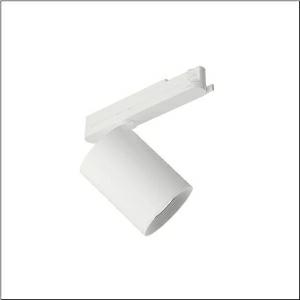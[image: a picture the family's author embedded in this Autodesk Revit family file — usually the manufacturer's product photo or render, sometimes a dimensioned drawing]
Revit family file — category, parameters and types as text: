
# Revit family: spot_11_51sd14mbb5a
name_source: partatom
category: Lighting Fixtures
units: mm (PartAtom-declared; Revit-internal decimal feet)

## family parameters
Cut with Voids When Loaded = No
Host = Face
Light Source = No
Part Type = Normal
Room Calculation Point = No
Round Connector Dimension = Use Diameter
Shared = No

## types (1)
- --- (1 x LED, 7340 lm, 50.2 W, 3000K)
    Apparent Load = 50 VA
    CIE Flux Codes = 95 98 100 100 100
    Color Rendering = 90
    Color Temperature = 3000K
    Default Elevation = 1800 mm
    Description = Spot 11, directional spotlight, light control with lens, of PMMA, LED rated luminous flux: 5.630lm, light colour: 930, control gear: ECG Multilumen, with 3-phase adapter, mains connection: 220..240V, AC, 50/60Hz, of aluminium, traffic white (RAL 9016), length: 213mm, diameter: 105mm, protection rating (complete): IP20, insulation class (complete): insulation class I (protective earthing), certification: CE, impact resistance: IK02, permissible ambient temperature for indoor applications: -20..+40°C, packaging unit: 1 piece
    Height = 175 mm
    Lamp = 1 x LED
    Lamp Light Flux = 7340 lm
    Lamp Power = 50.2 W
    Lamp count = 1
    Length = 105 mm
    Luminous efficacy = 146 lm/W
    Manufacturer = Siteco
    ModVariant = No
    Model = 51SD14MBB5A
    Mounting Place = Ceiling
    Mounting Type = Pendant
    Number of Poles = 1
    OnlyDefault = Yes
    Power Factor = 1
    Product Name = Spot 11
    Product group = directional spotlight
    ProductGroupID = 906
    Protection Class = Protection class I
    Protection Degree = IP 20
    RLX_Detail_Level = 1
    RLX_Emergency_Light_Flux = 0 lm
    RLX_Emergency_Type = 0
    RLX_Emergency_Type_DB = No
    RlxData = <blob elided: 17669 chars, md5=f89fbd72>
    Socket = socket
    Standby Power = 0 W
    System Light Flux = 7340 lm
    System Power = 50 W
    Type Comments = factory setting: luminous flux: 100 % | (ON | ON | ON | ON) | 1050 mA
    Type Image = l_1006697.jpg
    URL = http://relux.com
    VarID = @adj_147482
    Voltage = 0 V
    Weight = 0.00 kg
    Width = 0 mm  [stored 0 ft]

note: [stored X ft] marks values corroborated as IEEE doubles in the binary element streams (Revit-internal decimal feet)

## geometry (parser evidence)
native form markers: Blend x4, Sweep x11
no freeform markers — native parametric forms only
